FCSTD DOCUMENT  (FreeCAD 0.19R24366 (Git))
Label: WindTurbine
License: All rights reserved
LicenseURL: http://en.wikipedia.org/wiki/All_rights_reserved
objects: App::Link×3, Spreadsheet::Sheet×1, App::Part×1
EXTERNAL_REF file=Master_of_Puppets.FCStd obj=Spreadsheet
EXTERNAL_REF file=Master_of_Puppets.FCStd obj=WindTurbine
EXTERNAL_REF file=YawBearing/YawBearing_Assembly.FCStd obj=Part
EXTERNAL_REF file=YawBearing/Extended/YawBearing_Extended_Assembly.FCStd obj=Part
EXTERNAL_REF file=Tail/Tail_Assembly.FCStd obj=Part
EXTERNAL_REF file=Alternator/Alternator.FCStd obj=Part

FEATURE [Spreadsheet::Sheet] Spreadsheet
  cells = A1=Inputs; A2=CalculatedWindTurbineShape; B2(CalculatedWindTurbineShape)==Master_of_Puppets#Spreadsheet.CalculatedWindTurbineShape; A3=AlternatorLinkPlacement; B3(AlternatorLinkPlacement)==Master_of_Puppets#WindTurbine.AlternatorLinkPlacement; A4=TailAssemblyLinkPlacement; B4(TailAssemblyLinkPlacement)==Master_of_Puppets#WindTurbine.TailAssemblyLinkPlacement; A5=YawBearingPlacement; B5(YawBearingPlacement)==Master_of_Puppets#WindTurbine.YawBearingPlacement; A6=YawBearing; A7=YawBearing_Assembly; B7(TShapeYawBearing)==<<YawBearing_Assembly>>#Part._self; A8=YawBearing_Extended_Assembly; B8(ExtendedYawBearing)==<<YawBearing_Extended_Assembly>>#Part._self; A9=YawBearing; B9(YawBearing)==CalculatedWindTurbineShape == <<T>> ? TShapeYawBearing : ExtendedYawBearing
FEATURE [App::Link] Link  label="YawBearing"
  LinkPlacement = pos=(-127.03,141.844,-125.15) rot=(0,1,0;1.5708rad)
  LinkTransform = true
  LinkedObject = -> <external YawBearing/YawBearing_Assembly.FCStd>#Part
  Placement = pos=(-127.03,141.844,-125.15) rot=(0,1,0;1.5708rad)
  expr: LinkedObject = Spreadsheet.YawBearing
  expr: LinkPlacement = Spreadsheet.YawBearingPlacement
FEATURE [App::Link] Link001  label="Tail_Assembly"
  LinkPlacement = pos=(-127.03,-142.5,-125.15) rot=(0.57735,0.57735,0.57735;4.18879rad)
  LinkTransform = true
  LinkedObject = -> <external Tail/Tail_Assembly.FCStd>#Part
  Placement = pos=(-127.03,-142.5,-125.15) rot=(0.57735,0.57735,0.57735;4.18879rad)
  expr: LinkPlacement = Spreadsheet.TailAssemblyLinkPlacement
FEATURE [App::Link] Link002  label="Alternator"
  LinkPlacement = pos=(10.2827,8.86116,0) rot=(0,0,1;0.069813rad)
  LinkTransform = true
  LinkedObject = -> <external Alternator/Alternator.FCStd>#Part
  Placement = pos=(10.2827,8.86116,0) rot=(0,0,1;0.069813rad)
  expr: LinkPlacement = Spreadsheet.AlternatorLinkPlacement
FEATURE [App::Part] Part  label="WindTurbine"
  Group = -> [Link002,Link,Link001]
  Origin = -> Origin

RESOLVED EXTERNAL PARTS (link-assembly join: the EXTERNAL_REF files above that resolve inside this repo's crawl, each included once):
---- part Alternator/Alternator.FCStd = doc fcstd_aa6479d0f2e1 ----
FCSTD DOCUMENT  (FreeCAD 1.0R39109 (Git))
Label: Alternator
License: All rights reserved
LicenseURL: http://en.wikipedia.org/wiki/All_rights_reserved
objects: App::Link×9, Spreadsheet::Sheet×1, App::Part×1
EXTERNAL_REF file=../Master_of_Puppets.FCStd obj=Alternator
EXTERNAL_REF file=../Master_of_Puppets.FCStd obj=Blade
EXTERNAL_REF file=../Master_of_Puppets.FCStd obj=Fastener
EXTERNAL_REF file=../Master_of_Puppets.FCStd obj=Hub
EXTERNAL_REF file=../Master_of_Puppets.FCStd obj=Spreadsheet
EXTERNAL_REF file=Rotor/Rotor_Disk_Front.FCStd obj=Body
EXTERNAL_REF file=Rotor/Rotor_Front.FCStd obj=Part
EXTERNAL_REF file=Rotor/Rotor_Back.FCStd obj=Part
EXTERNAL_REF file=Stator/Stator.FCStd obj=Part
EXTERNAL_REF file=Hub/Hub.FCStd obj=Part
EXTERNAL_REF file=Studs/Studs_Hub.FCStd obj=Array
EXTERNAL_REF file=Frame/Frame.FCStd obj=Link
EXTERNAL_REF file=Studs/Studs_Frame.FCStd obj=Array
EXTERNAL_REF file=../Blades/Blade_Assembly_BackDisk.FCStd obj=Body
EXTERNAL_REF file=../Blades/Blade_Assembly_FrontTriangle.FCStd obj=Body

FEATURE [Spreadsheet::Sheet] Spreadsheet
  cells = A1='Inputs; A2='StatorThickness; B2='MechanicalClearance; C2='MagnetThickness; A3(StatorThickness)==Master_of_Puppets#Spreadsheet.StatorThickness; B3(MechanicalClearance)==Master_of_Puppets#Spreadsheet.MechanicalClearance; C3(MagnetThickness)==Master_of_Puppets#Spreadsheet.MagnetThickness; A4='RotorDiskThickness; B4='RotorDiskRadius; C4='HubHexNutThickness; A5(RotorDiskThickness)==Master_of_Puppets#Spreadsheet.RotorDiskThickness; B5(RotorDiskRadius)==Master_of_Puppets#Spreadsheet.RotorDiskRadius; C5(HubHexNutThickness)==Master_of_Puppets#Fastener.HubHexNutThickness; A6='DistanceThreadsExtendFromNuts; B6='WasherThickness; C6='BladeAssemblyPlateThickness; A7(DistanceThreadsExtendFromNuts)==Master_of_Puppets#Fastener.DistanceThreadsExtendFromNuts; B7(WasherThickness)==Master_of_Puppets#Fastener.WasherThickness; C7(BladeAssemblyPlateThickness)==Master_of_Puppets#Blade.BladeAssemblyPlateThickness; A8='BladeThickness; B8='HubStudsLength; C8='FramePlacement; A9(BladeThickness)==Master_of_Puppets#Blade.BladeThickness; B9(HubStudsLength)==Master_of_Puppets#Alternator.HubStudsLength; C9(FramePlacement)==Master_of_Puppets#Alternator.FramePlacement; A10='RotorTopology; B10='FrontRotorCount; C10='FrontRotorThickness; A11(RotorTopology)==Master_of_Puppets#Spreadsheet.RotorTopology; B11(FrontRotorCount)==Master_of_Puppets#Alternator.FrontRotorCount; C11(FrontRotorThickness)==Master_of_Puppets#Alternator.FrontRotorThickness; A12='Alternator; A13='Placement; B13(AlternatorPlacement)==Master_of_Puppets#Alternator.AlternatorPlacement; A14='RotorThickness; B14(RotorThickness)==Master_of_Puppets#Alternator.RotorThickness; A15='StatorResinCast; A16='StatorResinCastZ; B16(StatorResinCastZ)==-StatorThickness / 2; A17='RotorDisk; A18='FrontRotorDiskZ; B18(FrontRotorDiskZ)==StatorResinCastZ - MechanicalClearance * FrontRotorCount - FrontRotorThickness; A19='BackRotorDiskScale; B19(BackRotorDiskScale)==RotorTopology == <<Single>> ? -1 : 1; C19='Don't use scale due to 3d visualization OBJ export; A20='BackRotorDiskZ; B20(BackRotorDiskZ)==(MechanicalClearance - StatorResinCastZ + RotorThickness) * BackRotorDiskScale; A21='BackRotorDiskAngle; B21(BackRotorDiskAngle)==RotorTopology == <<Single>> ? 0 deg : 180 deg; A22='Hub; A23='FlangeMiddlePadThickness; B23(FlangeMiddlePadThickness)==Master_of_Puppets#Hub.MiddlePadThickness; A24='RotorSidePadWidth; B24(RotorSidePadWidth)==Master_of_Puppets#Hub.RotorSidePadWidth; A25='HubZ; B25(HubZ)==RotorTopology == <<Single>> ? BackRotorDiskZ - FlangeMiddlePadThickness : StatorThickness / 2 + RotorDiskThickness + MagnetThickness + MechanicalClearance; A26='HubStudsZ; B26(HubStudsZ)==(RotorTopology == <<Single>> ? BackRotorDiskZ + RotorDiskThickness : HubZ + FlangeMiddlePadThickness + DistanceThreadsExtendFromNuts) - HubStudsLength + HubHexNutThickness; A27='StatorMountingStuds; A28='X; B28='Y; C28='Z; A29(StatorMountingStudsX)=0; B29(StatorMountingStudsY)=0; C29(StatorMountingStudsZ)==.FramePlacement.Base.z; A30='BladeAssembly; A31='BackDiskZ; B31='FrontTriangleZ; A32(BladeAssemblyBackDiskZ)==RotorTopology == <<Single>> ? HubZ - BladeAssemblyPlateThickness : FrontRotorDiskZ - HubHexNutThickness - WasherThickness - BladeAssemblyPlateThickness; B32(FrontTriangleZ)==BladeAssemblyBackDiskZ - BladeThickness - BladeAssemblyPlateThickness; A33='RotorFrontLink; A34(RotorFrontLink)==RotorTopology == <<Single and metal disk>> ? Rotor_Disk_Front#<<Rotor_Disk_Front>>._self : Rotor_Front#<<Rotor>>._self
FEATURE [App::Link] Link001  label="Rotor_Front"
  LinkPlacement = pos=(0,0,-5) rot=(0,0,1;0rad)
  LinkedObject = -> <external Rotor/Rotor_Front.FCStd>#Part
  Placement = pos=(0,0,-5) rot=(0,0,1;0rad)
  expr: .Placement.Base.z = Spreadsheet.FrontRotorDiskZ
  expr: LinkedObject = Spreadsheet.RotorFrontLink
  expr: Visibility = Spreadsheet.FrontRotorCount
FEATURE [App::Link] Link002  label="Rotor_Back"
  LinkPlacement = pos=(0,0,-24) rot=(0,1,0;0rad)
  LinkedObject = -> <external Rotor/Rotor_Back.FCStd>#Part
  Placement = pos=(0,0,-24) rot=(0,1,0;0rad)
  expr: .Placement.Base.z = Spreadsheet.BackRotorDiskZ
  expr: .Placement.Rotation.Angle = Spreadsheet.BackRotorDiskAngle
FEATURE [App::Link] Link003  label="Stator"
  LinkPlacement = pos=(0,0,-5) rot=(0,0,1;0rad)
  LinkedObject = -> <external Stator/Stator.FCStd>#Part
  Placement = pos=(0,0,-5) rot=(0,0,1;0rad)
  expr: .LinkPlacement.Base.z = Spreadsheet.StatorResinCastZ
  expr: .Placement.Base.z = Spreadsheet.StatorResinCastZ
FEATURE [App::Link] Link  label="Hub"
  LinkPlacement = pos=(0,0,-40) rot=(0,0,1;0rad)
  LinkedObject = -> <external Hub/Hub.FCStd>#Part
  Placement = pos=(0,0,-40) rot=(0,0,1;0rad)
  expr: .Placement.Base.z = Spreadsheet.HubZ
FEATURE [App::Link] Link004  label="Studs_Hub"
  LinkPlacement = pos=(0,0,-107.41) rot=(0,0,1;0rad)
  LinkedObject = -> <external Studs/Studs_Hub.FCStd>#Array
  Placement = pos=(0,0,-107.41) rot=(0,0,1;0rad)
  expr: .Placement.Base.z = Spreadsheet.HubStudsZ
FEATURE [App::Link] Link005  label="Frame"
  LinkPlacement = pos=(0,0,66.32) rot=(0,0,1;0rad)
  LinkTransform = true
  LinkedObject = -> <external Frame/Frame.FCStd>#Link
  Placement = pos=(0,0,66.32) rot=(0,0,1;0rad)
  expr: LinkPlacement = Spreadsheet.FramePlacement
FEATURE [App::Link] Link006  label="Studs_Frame"
  LinkPlacement = pos=(0,0,66.32) rot=(0,0,1;0rad)
  LinkTransform = true
  LinkedObject = -> <external Studs/Studs_Frame.FCStd>#Array
  Placement = pos=(0,0,66.32) rot=(0,0,1;0rad)
  expr: .LinkPlacement.Base.x = Spreadsheet.StatorMountingStudsX
  expr: .LinkPlacement.Base.y = Spreadsheet.StatorMountingStudsY
  expr: .LinkPlacement.Base.z = Spreadsheet.StatorMountingStudsZ
FEATURE [App::Link] Link007  label="Blade_Assembly_BackDisk"
  LinkPlacement = pos=(0,0,-49) rot=(0,0,1;0rad)
  LinkedObject = -> <external ../Blades/Blade_Assembly_BackDisk.FCStd>#Body
  Placement = pos=(0,0,-49) rot=(0,0,1;0rad)
  expr: .Placement.Base.z = Spreadsheet.BladeAssemblyBackDiskZ
FEATURE [App::Link] Link008  label="Blade_Assembly_FrontTriangle"
  LinkPlacement = pos=(0,0,-93) rot=(0,0,1;0rad)
  LinkTransform = true
  LinkedObject = -> <external ../Blades/Blade_Assembly_FrontTriangle.FCStd>#Body
  Placement = pos=(0,0,-93) rot=(0,0,1;0rad)
  expr: .Placement.Base.z = Spreadsheet.FrontTriangleZ
FEATURE [App::Part] Part  label="Alternator"
  Group = -> [Link003,Link002,Link001,Link,Link004,Link005,Link006,Link007,Link008]
  Origin = -> Origin
  Placement = pos=(0,0,0) rot=(0.57735,-0.57735,-0.57735;2.0944rad)
  expr: Placement = Spreadsheet.AlternatorPlacement
---- part Master_of_Puppets.FCStd = doc fcstd_6404554055c4 (61625 chars; too large to inline — full recipe in that document) ----
---- part Tail/Tail_Assembly.FCStd = doc fcstd_6504892cc698 ----
FCSTD DOCUMENT  (FreeCAD 0.20R29177 (Git))
Label: Tail_Assembly
License: All rights reserved
LicenseURL: http://en.wikipedia.org/wiki/All_rights_reserved
objects: App::Link×2, Spreadsheet::Sheet×1, App::Part×1
EXTERNAL_REF file=../Master_of_Puppets.FCStd obj=HighEndStop
EXTERNAL_REF file=Hinge/Inner/Tail_Hinge_Inner.FCStd obj=Part001
EXTERNAL_REF file=Tail.FCStd obj=Part

FEATURE [Spreadsheet::Sheet] Spreadsheet
  cells = A1=Inputs; A2=TailAssemblyPlacement; B2(TailAssemblyPlacement)==Master_of_Puppets#HighEndStop.TailAssemblyPlacement
FEATURE [App::Link] Link  label="Hinge_Inner"
  LinkedObject = -> <external Hinge/Inner/Tail_Hinge_Inner.FCStd>#Part001
FEATURE [App::Link] Link001  label="Tail"
  LinkTransform = true
  LinkedObject = -> <external Tail.FCStd>#Part
FEATURE [App::Part] Part  label="Tail_Assembly"
  Group = -> [Link,Link001]
  Origin = -> Origin
  Placement = pos=(-8.64666,-12.3487,0) rot=(0,0,-1;2.18166rad)
  expr: Placement = Spreadsheet.TailAssemblyPlacement
---- part YawBearing/Extended/YawBearing_Extended_Assembly.FCStd = doc fcstd_29229a6b5b82 ----
FCSTD DOCUMENT  (FreeCAD 1.0R39109 (Git))
Label: YawBearing_Extended_Assembly
License: All rights reserved
LicenseURL: http://en.wikipedia.org/wiki/All_rights_reserved
objects: App::Link×5, App::Part×2, Spreadsheet::Sheet×1
EXTERNAL_REF file=../YawBearing_Pipe.FCStd obj=Tube
EXTERNAL_REF file=YawBearing_Extended_Side.FCStd obj=Body
EXTERNAL_REF file=YawBearing_Extended_Top.FCStd obj=Body
EXTERNAL_REF file=../../Master_of_Puppets.FCStd obj=Alternator
EXTERNAL_REF file=../../Master_of_Puppets.FCStd obj=HighEndStop
EXTERNAL_REF file=../../Master_of_Puppets.FCStd obj=Spreadsheet
EXTERNAL_REF file=../../Master_of_Puppets.FCStd obj=YawBearing
EXTERNAL_REF file=../YawBearing_ArcWireSupport.FCStd obj=PadBody
EXTERNAL_REF file=../YawBearing_SafetyCatch.FCStd obj=Body

FEATURE [App::Link] Link  label="Pipe"
  LinkTransform = true
  LinkedObject = -> <external ../YawBearing_Pipe.FCStd>#Tube
FEATURE [App::Link] Link001  label="Side"
  LinkPlacement = pos=(19.5302,-101.25,-49.9296) rot=(0,1,0;0rad)
  LinkTransform = true
  LinkedObject = -> <external YawBearing_Extended_Side.FCStd>#Body
  Placement = pos=(19.5302,-101.25,-49.9296) rot=(0,1,0;0rad)
  expr: .LinkPlacement.Base.x = Spreadsheet.SideX
  expr: .LinkPlacement.Base.y = Spreadsheet.SideY
  expr: .LinkPlacement.Base.z = Spreadsheet.SideZ
  expr: .LinkPlacement.Rotation.Angle = Spreadsheet.SideYAngle
FEATURE [App::Link] Link002  label="Top"
  LinkPlacement = pos=(-44.45,10,-49.9296) rot=(0,0,1;0rad)
  LinkedObject = -> <external YawBearing_Extended_Top.FCStd>#Body
  Placement = pos=(-44.45,10,-49.9296) rot=(0,0,1;0rad)
  expr: Placement = Spreadsheet.ExtendedTopPlacement
FEATURE [Spreadsheet::Sheet] Spreadsheet
  cells = A1='Inputs; A2='YawPipeDiameter; B2(YawPipeDiameter)==Master_of_Puppets#Spreadsheet.YawPipeDiameter; A3='PipeThickness; B3(PipeThickness)==Master_of_Puppets#Spreadsheet.PipeThickness; A4='FlatMetalThickness; B4(FlatMetalThickness)==Master_of_Puppets#Spreadsheet.FlatMetalThickness; A5='Width; B5(Width)==Master_of_Puppets#YawBearing.MM; A6='RotorDiskRadius; B6(RotorDiskRadius)==Master_of_Puppets#Spreadsheet.RotorDiskRadius; A7='k; B7(k)==Master_of_Puppets#Alternator.k; A8='YawBearingPlateTopHoleRadius; B8(YawBearingPlateTopHoleRadius)==Master_of_Puppets#YawBearing.YawBearingPlateTopHoleRadius; A9='SafetyCatchZ; B9(SafetyCatchZ)==Master_of_Puppets#HighEndStop.SafetyCatchZ; A10='SafetyCatchPartAngle; B10(SafetyCatchPartAngle)==Master_of_Puppets#HighEndStop.SafetyCatchAngle; A11='YawPipeLength; B11(YawPipeLength)==Master_of_Puppets#HighEndStop.YawPipeLength; A12='TopAngle; B12(TopAngle)==Master_of_Puppets#YawBearing.TopAngle; A13='YawPipeRadius; B13(YawPipeRadius)==Master_of_Puppets#YawBearing.YawPipeRadius; A14='HalfWidth; B14(HalfWidth)==Master_of_Puppets#YawBearing.HalfWidth; A15='ArcWireSupportLength; B15(ArcWireSupportLength)==Master_of_Puppets#YawBearing.ArcWireSupportLength; A16='SideYAngle; B16(SideYAngle)==Master_of_Puppets#YawBearing.SideYAngle; A17='ExtendedTopPlacement; B17(ExtendedTopPlacement)==Master_of_Puppets#YawBearing.ExtendedTopPlacement; A18='ArcWireSupport; A19='Offset; B19(Offset)==sqrt((ArcWireSupportLength / 2) ^ 2 / 2); C19='from a^2 + b^2 = c^2; A20='X; B20='Y; C20='Z; A21(ArcWireSupportX)==YawBearingPlateTopHoleRadius * cos(45) + Offset; B21(ArcWireSupportY)==FlatMetalThickness; C21(ArcWireSupportZ)==YawBearingPlateTopHoleRadius * sin(45) + Offset; A22='Side; A23='X; B23='Y; C23='Z; A24(SideX)==Master_of_Puppets#YawBearing.SideX; B24(SideY)==Master_of_Puppets#YawBearing.SideY; C24(SideZ)==Master_of_Puppets#YawBearing.SideZ; A25='SafetyCatch; A26='Rotation; B26='Axis; C26='Angle; A27(SafetyCatchRotation)==create(<<rotation>>; 0; TopAngle; 90); B27(SafetyCatchAxis)==.SafetyCatchRotation.Axis; C27(SafetyCatchAngle)==.SafetyCatchRotation.Angle * 180 / pi; A28='SafetyCatchLinkY; B28(SafetyCatchLinkY)==(YawPipeLength - SafetyCatchZ) * -1
FEATURE [App::Link] Link003  label="ArcWireSupport"
  LinkPlacement = pos=(29.3842,10,29.3842) rot=(0,1,0;2.35619rad)
  LinkedObject = -> <external ../YawBearing_ArcWireSupport.FCStd>#PadBody
  Placement = pos=(29.3842,10,29.3842) rot=(0,1,0;2.35619rad)
  expr: .Placement.Base.x = Spreadsheet.ArcWireSupportX
  expr: .Placement.Base.y = Spreadsheet.ArcWireSupportY
  expr: .Placement.Base.z = Spreadsheet.ArcWireSupportZ
FEATURE [App::Link] Link004  label="SafetyCatch"
  LinkPlacement = pos=(0,-12.1663,0) rot=(0.862856,0.357407,-0.357407;1.71777rad)
  LinkedObject = -> <external ../YawBearing_SafetyCatch.FCStd>#Body
  Placement = pos=(0,-12.1663,0) rot=(0.862856,0.357407,-0.357407;1.71777rad)
  expr: .LinkPlacement.Base.y = Spreadsheet.SafetyCatchLinkY
  expr: .LinkPlacement.Rotation.Angle = Spreadsheet.SafetyCatchAngle
  expr: .LinkPlacement.Rotation.Axis = Spreadsheet.SafetyCatchAxis
  expr: .Placement.Base.y = Spreadsheet.SafetyCatchLinkY
  expr: .Placement.Rotation.Angle = Spreadsheet.SafetyCatchAngle
  expr: .Placement.Rotation.Axis = Spreadsheet.SafetyCatchAxis
FEATURE [App::Part] Part001  label="SafetyCatchPart"
  Group = -> [Link004]
  Origin = -> Origin001
  Placement = pos=(0,0,0) rot=(0,-1,0;0.062891rad)
  expr: .Placement.Rotation.Angle = Spreadsheet.SafetyCatchPartAngle
FEATURE [App::Part] Part  label="YawBearing_Extended_Assembly"
  Group = -> [Link001,Link002,Link,Link003,Part001]
  Origin = -> Origin
---- part YawBearing/YawBearing_Assembly.FCStd = doc fcstd_0fa34e46f127 ----
FCSTD DOCUMENT  (FreeCAD 0.21R33771 (Git))
Label: YawBearing_Assembly
License: All rights reserved
LicenseURL: http://en.wikipedia.org/wiki/All_rights_reserved
objects: App::Link×4, App::Part×2, Spreadsheet::Sheet×1
EXTERNAL_REF file=YawBearing_Pipe.FCStd obj=Tube
EXTERNAL_REF file=YawBearing_Plate_Top.FCStd obj=PocketBody
EXTERNAL_REF file=../Master_of_Puppets.FCStd obj=Alternator
EXTERNAL_REF file=../Master_of_Puppets.FCStd obj=HighEndStop
EXTERNAL_REF file=../Master_of_Puppets.FCStd obj=Spreadsheet
EXTERNAL_REF file=../Master_of_Puppets.FCStd obj=YawBearing
EXTERNAL_REF file=YawBearing_ArcWireSupport.FCStd obj=PadBody
EXTERNAL_REF file=YawBearing_SafetyCatch.FCStd obj=Body

FEATURE [App::Link] Link  label="Pipe"
  LinkTransform = true
  LinkedObject = -> <external YawBearing_Pipe.FCStd>#Tube
FEATURE [App::Link] Link001  label="Plate_Top"
  LinkPlacement = pos=(-3.525,0,5.995) rot=(1,0,0;-1.5708rad)
  LinkedObject = -> <external YawBearing_Plate_Top.FCStd>#PocketBody
  Placement = pos=(-3.525,0,5.995) rot=(1,0,0;-1.5708rad)
  expr: .Placement.Base.x = Spreadsheet.TopPlateX
  expr: .Placement.Base.z = Spreadsheet.TopPlateZ
FEATURE [Spreadsheet::Sheet] Spreadsheet
  cells = A1='Inputs; A2='YawPipeDiameter; B2(YawPipeDiameter)==Master_of_Puppets#Spreadsheet.YawPipeDiameter; A3='FlatMetalThickness; B3(FlatMetalThickness)==Master_of_Puppets#Spreadsheet.FlatMetalThickness; A4='I; B4(I)==Master_of_Puppets#Alternator.I; A5='k; B5(k)==Master_of_Puppets#Alternator.k; A6='YawBearingPlateTopHoleRadius; B6(YawBearingPlateTopHoleRadius)==Master_of_Puppets#YawBearing.YawBearingPlateTopHoleRadius; A7='SafetyCatchZ; B7(SafetyCatchZ)==Master_of_Puppets#HighEndStop.SafetyCatchZ; A8='SafetyCatchPartAngle; B8(SafetyCatchPartAngle)==Master_of_Puppets#HighEndStop.SafetyCatchAngle; A9='YawPipeLength; B9(YawPipeLength)==Master_of_Puppets#HighEndStop.YawPipeLength; A10='ArcWireSupportLength; B10(ArcWireSupportLength)==Master_of_Puppets#YawBearing.ArcWireSupportLength; A11='Calculated; A12='TopPlateX; B12(TopPlateX)==-I / 2; A13='TopPlateZ; B13(TopPlateZ)==k / 2; A14='ArcWireSupportX; B14(ArcWireSupportX)==-ArcWireSupportLength / 2 - YawBearingPlateTopHoleRadius; A15='ArcWireSupportY; B15(ArcWireSupportY)==FlatMetalThickness; A16='SafetyCatchLinkY; B16(SafetyCatchLinkY)==(YawPipeLength - SafetyCatchZ) * -1; A17='SafetyCatchRotation; B17(SafetyCatchRotation)==create(<<rotation>>; 0; -90; 90); A18='SafetyCatchAxis; B18(SafetyCatchAxis)==.SafetyCatchRotation.Axis; A19='SafetyCatchAngle; B19(SafetyCatchAngle)==.SafetyCatchRotation.Angle * 180 / pi
FEATURE [App::Link] Link002  label="ArcWireSupport"
  LinkPlacement = pos=(-20.6,5,0) rot=(0,0,1;0rad)
  LinkedObject = -> <external YawBearing_ArcWireSupport.FCStd>#PadBody
  Placement = pos=(-20.6,5,0) rot=(0,0,1;0rad)
  expr: .Placement.Base.x = -Spreadsheet.ArcWireSupportLength / 2 - Spreadsheet.YawBearingPlateTopHoleRadius
  expr: .Placement.Base.y = Spreadsheet.ArcWireSupportY
FEATURE [App::Link] Link003  label="SafetyCatch"
  LinkPlacement = pos=(0,-22.4398,0) rot=(0.57735,-0.57735,0.57735;2.0944rad)
  LinkedObject = -> <external YawBearing_SafetyCatch.FCStd>#Body
  Placement = pos=(0,-22.4398,0) rot=(0.57735,-0.57735,0.57735;2.0944rad)
  expr: .LinkPlacement.Base.y = Spreadsheet.SafetyCatchLinkY
  expr: .Placement.Rotation.Angle = Spreadsheet.SafetyCatchAngle
  expr: .Placement.Rotation.Axis = Spreadsheet.SafetyCatchAxis
FEATURE [App::Part] Part001  label="SafetyCatchPart"
  Group = -> [Link003]
  Origin = -> Origin001
  Placement = pos=(0,0,0) rot=(0,-1,0;0.066334rad)
  expr: .Placement.Rotation.Angle = Spreadsheet.SafetyCatchPartAngle
FEATURE [App::Part] Part  label="YawBearing_Assembly"
  Group = -> [Link,Link001,Link002,Part001]
  Origin = -> Origin
